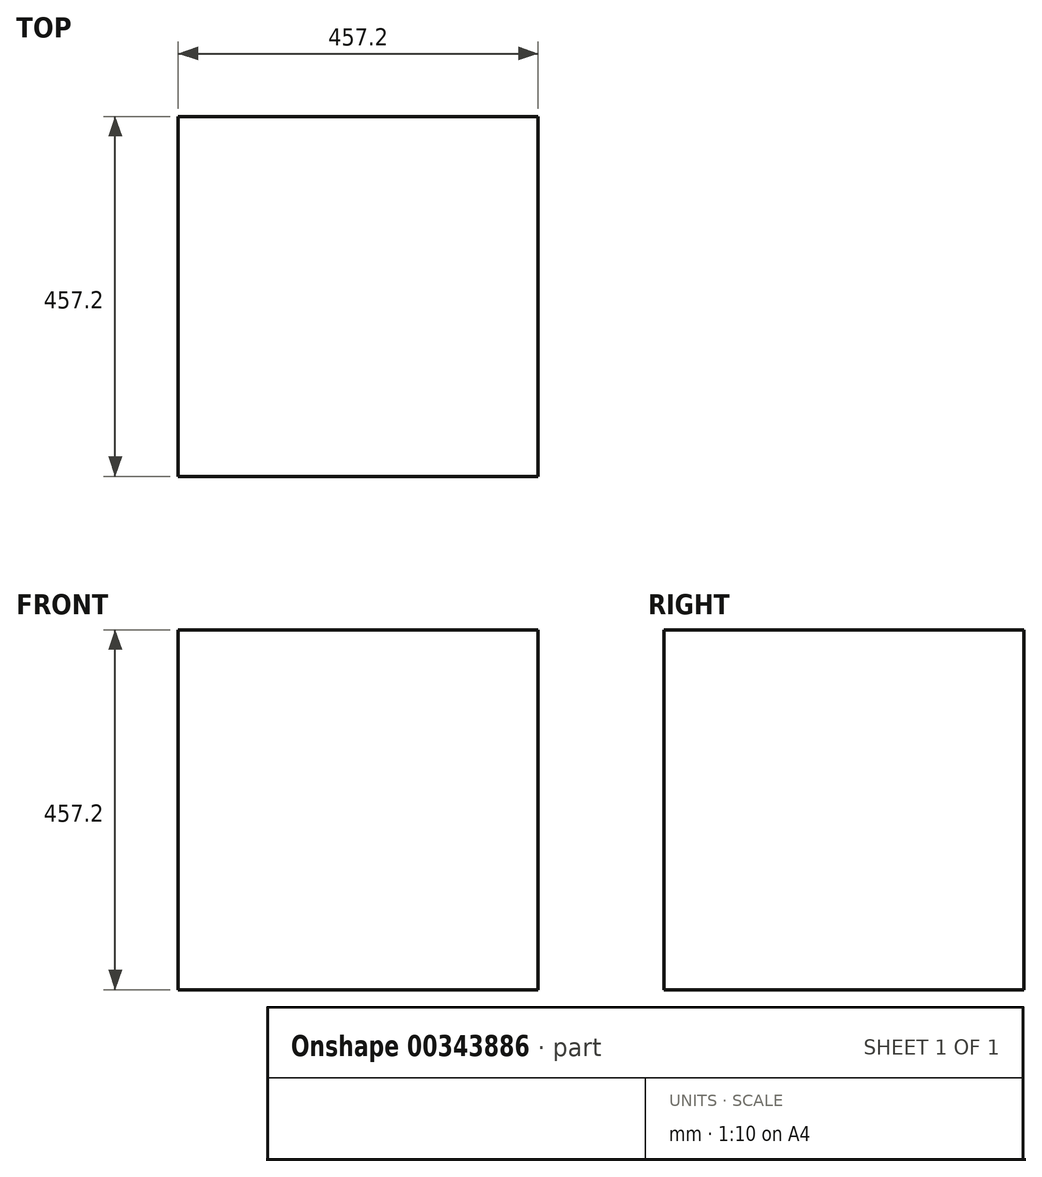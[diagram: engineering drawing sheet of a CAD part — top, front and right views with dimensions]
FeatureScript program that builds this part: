
annotation { "Feature Type Name" : "Feature", "Feature Type Description" : "" }
export const myFeature = defineFeature(function(context is Context, id is Id, definition is map)
    precondition{}
    {
        {
            var Q0;
            Q0=qCreatedBy(makeId("Top.planeOp"),FACE);
            var sketch = newSketch(context, id + "F0", { "sketchPlane" : qUnion([Q0])});
            skLineSegment(sketch, "E0.bottom", {"start": v(-401.16, 405.68) * mm, "end": v(56.04, 405.68) * mm});
            skLineSegment(sketch, "E0.top", {"start": v(-401.16, -51.52) * mm, "end": v(56.04, -51.52) * mm});
            skLineSegment(sketch, "E0.left", {"start": v(-401.16, 405.68) * mm, "end": v(-401.16, -51.52) * mm});
            skLineSegment(sketch, "E0.right", {"start": v(56.04, 405.68) * mm, "end": v(56.04, -51.52) * mm});
            skSolve(sketch);
        }
        {
            var Q0;
            Q0=makeQuery(id+"F0.imprint","IMPRINT",FACE,{"disambiguationData":[TD([[makeQuery(id+"F0.imprint","IMPRINT",EDGE,{"derivedFrom":sQuery(id+"F0.wireOp",EDGE,"E0.bottom")}),-1.0]])]});
            extrude(context, id + "F1", {"entities" : qUnion([Q0]), "depth" : 457.2 * mm});
        }
    });
